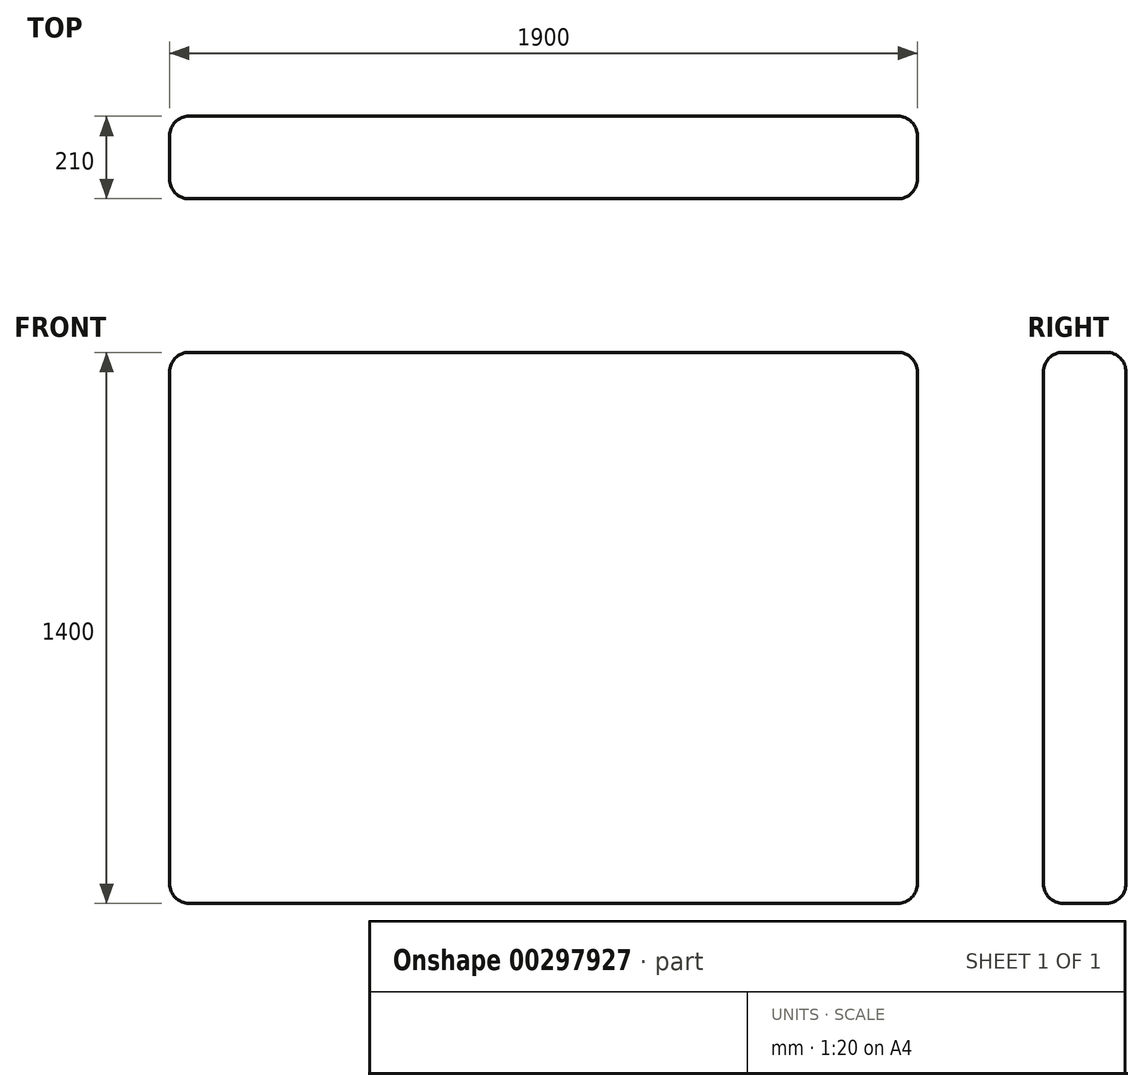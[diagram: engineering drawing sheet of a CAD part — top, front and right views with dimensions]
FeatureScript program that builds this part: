
annotation { "Feature Type Name" : "Feature", "Feature Type Description" : "" }
export const myFeature = defineFeature(function(context is Context, id is Id, definition is map)
    precondition{}
    {
        {
            var Q0;
            Q0=qCreatedBy(makeId("Front.planeOp"),FACE);
            var sketch = newSketch(context, id + "F0", { "sketchPlane" : qUnion([Q0])});
            skLineSegment(sketch, "E0.bottom", {"start": v(-1000, 700) * mm, "end": v(900, 700) * mm});
            skLineSegment(sketch, "E0.top", {"start": v(-1000, -700) * mm, "end": v(900, -700) * mm});
            skLineSegment(sketch, "E0.left", {"start": v(-1000, 700) * mm, "end": v(-1000, -700) * mm});
            skLineSegment(sketch, "E0.right", {"start": v(900, 700) * mm, "end": v(900, -700) * mm});
            skSolve(sketch);
        }
        {
            var Q0;
            Q0=makeQuery(id+"F0.imprint","IMPRINT",FACE,{"disambiguationData":[TD([[makeQuery(id+"F0.imprint","IMPRINT",EDGE,{"derivedFrom":sQuery(id+"F0.wireOp",EDGE,"E0.bottom")}),-1.0]])]});
            extrude(context, id + "F1", {"entities" : qUnion([Q0]), "endBound" : BoundingType.SYMMETRIC, "depth" : 210 * mm});
        }
        {
            var Q0;
            Q0=makeQuery(id+"F1.opExtrude","SWEPT_EDGE",EDGE,{"disambiguationData":[OSD([sQuery(id+"F0.wireOp",EDGE,"E0.bottom"),sQuery(id+"F0.wireOp",EDGE,"E0.left")])]});
            var Q1;
            Q1=makeQuery(id+"F1.opExtrude","SWEPT_EDGE",EDGE,{"disambiguationData":[OSD([sQuery(id+"F0.wireOp",EDGE,"E0.bottom"),sQuery(id+"F0.wireOp",EDGE,"E0.right")])]});
            var Q2;
            Q2=makeQuery(id+"F1.opExtrude","SWEPT_EDGE",EDGE,{"disambiguationData":[OSD([sQuery(id+"F0.wireOp",EDGE,"E0.top"),sQuery(id+"F0.wireOp",EDGE,"E0.right")])]});
            var Q3;
            Q3=makeQuery(id+"F1.opExtrude","SWEPT_EDGE",EDGE,{"disambiguationData":[OSD([sQuery(id+"F0.wireOp",EDGE,"E0.top"),sQuery(id+"F0.wireOp",EDGE,"E0.left")])]});
            fillet(context, id + "F2", {"entities" : qUnion([Q0, Q1, Q2, Q3]), "radius" : 50 * mm, "tangentPropagation" : true, "allowEdgeOverflow" : false});
        }
        {
            var Q0;
            Q0=makeQuery(id+"F1.opExtrude","CAP_FACE",FACE,{"disambiguationData":[OSD([sQuery(id+"F0.wireOp",EDGE,"E0.bottom"),sQuery(id+"F0.wireOp",EDGE,"E0.top"),sQuery(id+"F0.wireOp",EDGE,"E0.left"),sQuery(id+"F0.wireOp",EDGE,"E0.right")])],"isStart":false});
            var Q1;
            Q1=makeQuery(id+"F1.opExtrude","CAP_FACE",FACE,{"disambiguationData":[OSD([sQuery(id+"F0.wireOp",EDGE,"E0.bottom"),sQuery(id+"F0.wireOp",EDGE,"E0.top"),sQuery(id+"F0.wireOp",EDGE,"E0.left"),sQuery(id+"F0.wireOp",EDGE,"E0.right")])],"isStart":true});
            fillet(context, id + "F3", {"entities" : qUnion([Q0, Q1]), "radius" : 50 * mm, "tangentPropagation" : true, "allowEdgeOverflow" : false});
        }
    });
